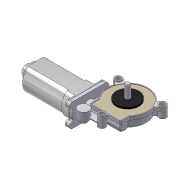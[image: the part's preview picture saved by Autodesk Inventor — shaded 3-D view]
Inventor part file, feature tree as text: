
AUTODESK INVENTOR PART (.ipt)
format: ipt  version: 2014 (Build 180170000, 170)  size: 626,176 bytes
history: native  units: mm
features: sketch x28, extrude x24, fillet x7, projected_geometry x5, rib x4, other x3, chamfer x2, plane x2, pattern_circular x1, hole x1
ambient origin geometry x8: Origin, YZ Plane, XZ Plane, XY Plane, X Axis, Y Axis, Z Axis, Center Point
bodies: Solid1 (feature_tree)
feature tree (77):
  extrude  "Extrusion1"  Depth=50.0mm
  extrude  "Extrusion2"  Depth=5.6mm TaperAngle=0.0deg
  extrude  "Extrusion3"  Depth=12.3mm TaperAngle=0.0deg
  extrude  "Extrusion4"  Depth=1.5mm TaperAngle=0.0deg
  extrude  "Extrusion5"  Depth=2.0mm TaperAngle=0.0deg
  extrude  "Extrusion6"  Depth=10.0mm
  rib  "Rib1"
  fillet  "Fillet1"  Radius=1.0mm
  pattern_circular  "Circular Pattern1"  Count=8 Angle=360.0deg
  extrude  "Extrusion9"  Depth=0.3mm
  extrude  "Extrusion7"  Depth=36.27mm
  extrude  "Extrusion8"  Depth=20.98mm
  rib  "Rib2"
  extrude  "Extrusion10"  Depth=10.5mm TaperAngle=0.0deg
  hole  "Hole2"  [1 undecoded]
  chamfer  "Chamfer1"  Distance=0.5mm
  extrude  "Extrusion11"  Depth=2.0mm TaperAngle=45.0deg
  extrude  "Extrusion12"  Depth=3.5mm TaperAngle=0.0deg
  chamfer  "Chamfer2"  Distance=20.0mm
  extrude  "Extrusion13"  Depth=2.0mm TaperAngle=45.0deg
  plane  "Work Plane1"
  extrude  "Extrusion14"  Depth=10.0mm
  fillet  "Fillet2"  Radius=30.0mm
  sketch  "Sketch20"  dims[d62=37.25mm d63=3.5mm d64=0.0mm d65=20.0mm d66=0.0mm]
  extrude  "Extrusion15"  [1 undecoded]
  extrude  "Extrusion17"  Depth=9.9mm
  extrude  "Extrusion18"  Depth=5.0mm TaperAngle=0.0deg
  extrude  "Extrusion19"  Depth=5.0mm
  extrude  "Extrusion20"  Depth=64.0mm
  extrude  "Extrusion21"  Depth=2.0mm TaperAngle=0.0deg
  fillet  "Fillet3"  Radius=48.8mm
  extrude  "Extrusion22"  Depth=45.5mm
  other  "Work Axis1"
  plane  "Work Plane3"
  rib  "Rib3"
  sketch  "Sketch30"  dims[d88=0.5mm d89=0.0mm d92=2.0mm d93=0.0mm d94=48.8mm]
  extrude  "Extrusion23"  Depth=2.0mm
  extrude  "Extrusion24"  Depth=2.0mm TaperAngle=0.0deg
  extrude  "Extrusion26"  Depth=2.0mm
  rib  "Rib4"
  fillet  "Fillet4"  Radius=7.4mm
  fillet  "Fillet5"  Radius=1.5mm
  fillet  "Fillet6"  Radius=18.0mm
  fillet  "Fillet7"  Radius=10.0mm
  other  "Emboss_LH"
  sketch  "Sketch1"  dims[d0=67.0mm d1=50.0mm]
  sketch  "Sketch2"  dims[d2=37.0mm d3=5.6mm d4=0.0mm]
  sketch  "Sketch3"  dims[d5=3.0mm d6=12.3mm d7=0.0mm]
  sketch  "Sketch4"  dims[d8=42.0mm d9=1.5mm d10=0.0mm]
  sketch  "Sketch5"  dims[d11=21.0mm d12=2.0mm d13=0.0mm]
  sketch  "Sketch6"  dims[d14=8.75mm d15=0.0mm d16=10.0mm d17=1.0mm d18=0.0mm]
  sketch  "Sketch7"  dims[d19=1.5mm]
  other  "embossLH"
  sketch  "Sketch9"  dims[d20=1.0mm]
  sketch  "Sketch10"  dims[d21=1.5mm d22=0.0mm d23=80.0mm d24=360.0deg]
  sketch  "Sketch11"  dims[d26=0.3mm d27=0.0mm d28=11.5mm]
  projected_geometry  "Projected Loop1"
  projected_geometry  "Projected Loop2"
  projected_geometry  "Projected Loop3"
  sketch  "Sketch13"  dims[d29=36.27mm d30=36.27mm]
  sketch  "Sketch14"  dims[d31=41.84mm d32=20.98mm]
  sketch  "Sketch15"  dims[d33=1.0mm d34=0.0mm d35=10.5mm d36=0.0mm]
  projected_geometry  "Projected Loop4"
  projected_geometry  "Projected Loop5"
  sketch  "Sketch16"  dims[d37=3.0mm d38=1.0mm d39=0.0mm]
  sketch  "Sketch17"  dims[d47=1.2mm d48=0.5mm d49=0.0mm]
  sketch  "Sketch18"  dims[d50=1.5mm d51=0.0mm]
  sketch  "Sketch19"  dims[d52=7.1mm d53=6.0mm d54=4.0mm d55=2.0mm d56=90.0deg d57=7.1mm d58=20.594885mm d59=0.7mm d60=2.0mm d61=45.0deg]
  sketch  "Sketch23"  dims[d67=7.95mm d68=0.7mm d69=2.0mm d70=45.0deg]
  sketch  "Sketch24"  dims[d71=10.0mm d72=14.0mm d73=30.0mm]
  sketch  "Sketch25"  dims[d74=20.0mm d75=0.0mm d76=-38.0mm]
  sketch  "Sketch26"  dims[d77=37.9mm d79=9.9mm]
  sketch  "Sketch27"  dims[d80=25.0mm d81=5.0mm d82=0.0mm]
  sketch  "Sketch28"  dims[d84=1.5mm d85=5.0mm]
  sketch  "Sketch29"  dims[d86=18.0mm d87=64.0mm]
  sketch  "Sketch31"  dims[d95=13.0mm d96=0.0mm d97=45.5mm]
  sketch  "Sketch33"  dims[d98=67.0mm d99=0.0mm d100=28.6mm d101=8.0mm d102=0.0mm d103=20.0mm d104=7.4mm d105=-2.617994mm d106=1.5mm d107=18.0mm d108=10.0mm d109=0.0mm d110=1.5mm d111=1.0mm d112=0.0mm d113=17.5mm d114=10.6mm d115=0.0mm d116=3.0mm d117=0.0mm d118=10.7mm d121=6.9mm d122=4.6mm d123=0.0mm d124=2.0mm d125=1.0mm d126=0.0mm d127=1.5mm d128=0.5mm d129=1.0mm d130=2.0mm d131=0.2mm d132=48.8mm d134=45.5mm]
note: 2 required parameter values undecoded (feature->parameter linkage not recoverable at this tier; creation-order binding heuristic only, values carry confidence <= 0.55)
